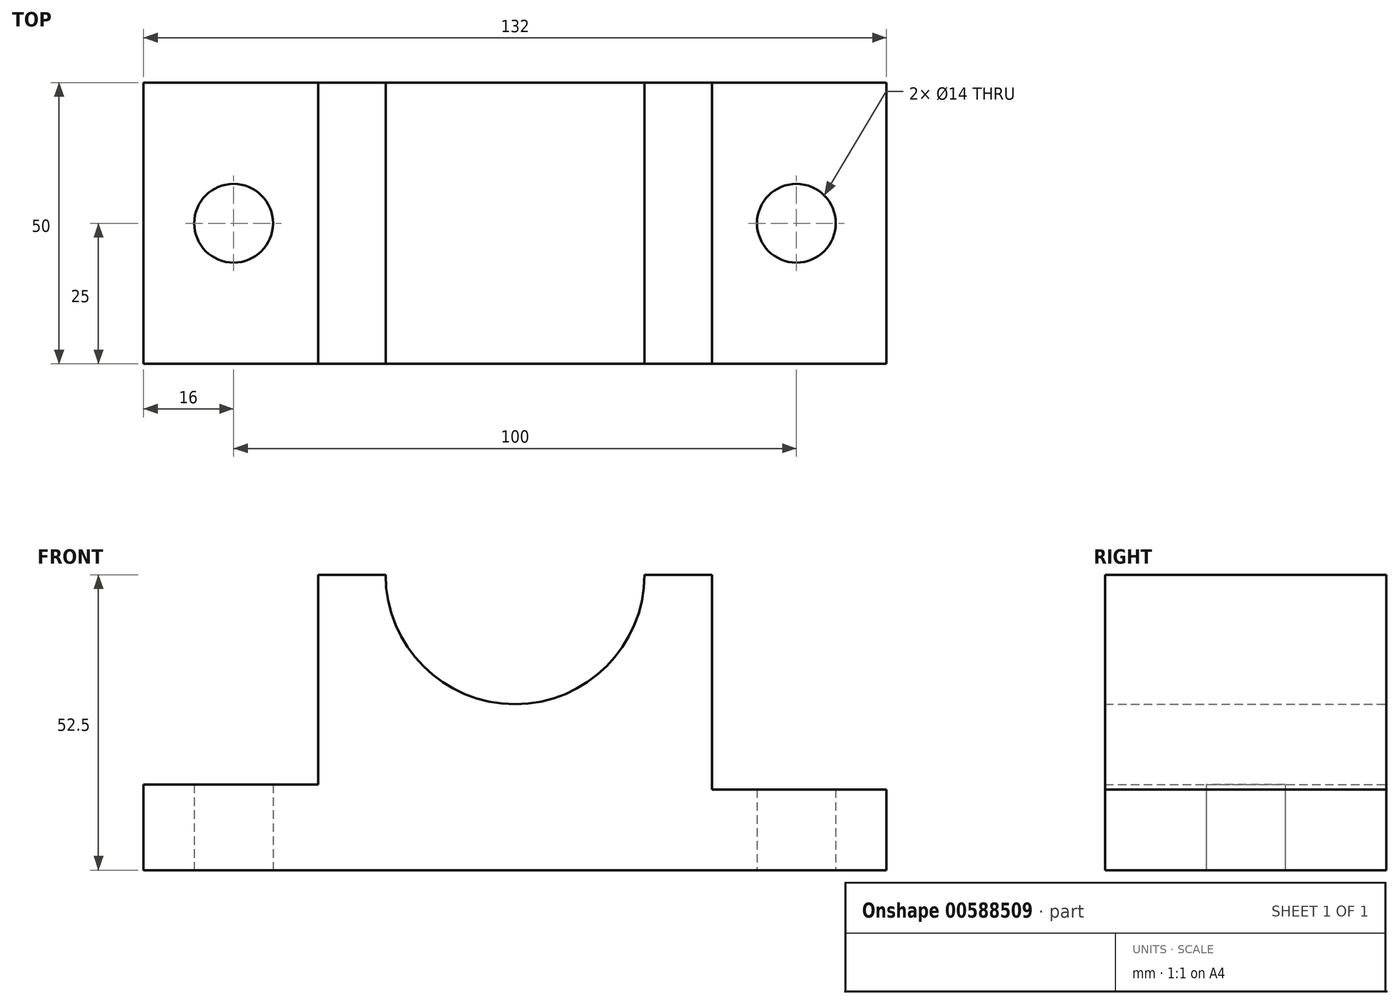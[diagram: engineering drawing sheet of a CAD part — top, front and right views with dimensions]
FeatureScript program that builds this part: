
annotation { "Feature Type Name" : "Feature", "Feature Type Description" : "" }
export const myFeature = defineFeature(function(context is Context, id is Id, definition is map)
    precondition{}
    {
        {
            var Q0;
            Q0=qCreatedBy(makeId("Front.planeOp"),FACE);
            var sketch = newSketch(context, id + "F0", { "sketchPlane" : qUnion([Q0])});
            skLineSegment(sketch, "E0", {"start": v(0, 0) * mm, "end": v(-66, 0) * mm});
            skLineSegment(sketch, "E1", {"start": v(-66, 0) * mm, "end": v(-66, 15.21) * mm});
            skLineSegment(sketch, "E2", {"start": v(-66, 15.21) * mm, "end": v(-35, 15.21) * mm});
            skLineSegment(sketch, "E3", {"start": v(-35, 15.21) * mm, "end": v(-35, 52.5) * mm});
            skLineSegment(sketch, "E4", {"start": v(-35, 52.5) * mm, "end": v(-23, 52.5) * mm});
            skLineSegment(sketch, "E5", {"start": v(23, 52.5) * mm, "end": v(35, 52.5) * mm});
            skLineSegment(sketch, "E6", {"start": v(35, 52.5) * mm, "end": v(35, 14.36) * mm});
            skLineSegment(sketch, "E7", {"start": v(35, 14.36) * mm, "end": v(66, 14.36) * mm});
            skLineSegment(sketch, "E8", {"start": v(66, 14.36) * mm, "end": v(66, 0) * mm});
            skLineSegment(sketch, "E9", {"start": v(66, 0) * mm, "end": v(0, 0) * mm});
            skArc(sketch, "E10", {"start": v(-23, 52.5) * mm, "mid": v(0, 29.5) * mm, "end": v(23, 52.5) * mm});
            skSolve(sketch);
        }
        {
            var Q0;
            Q0=makeQuery(id+"F0.imprint","IMPRINT",FACE,{"disambiguationData":[TD([[makeQuery(id+"F0.imprint","IMPRINT",EDGE,{"derivedFrom":sQuery(id+"F0.wireOp",EDGE,"E0")}),-1.0]])]});
            extrude(context, id + "F1", {"entities" : qUnion([Q0]), "depth" : 50 * mm, "offsetDistance" : 25 * mm});
        }
        {
            var Q0;
            Q0=qCreatedBy(makeId("Top.planeOp"),FACE);
            var sketch = newSketch(context, id + "F2", { "sketchPlane" : qUnion([Q0])});
            skCircle(sketch, "E11", {"center": v(-50, -25) * mm, "radius": 7 * mm});
            skCircle(sketch, "E12", {"center": v(50, -25) * mm, "radius": 7 * mm});
            skSolve(sketch);
        }
        {
            var Q0;
            Q0=makeQuery(id+"F2.imprint","IMPRINT",FACE,{"disambiguationData":[TD([[makeQuery(id+"F2.imprint","IMPRINT",EDGE,{"derivedFrom":sQuery(id+"F2.wireOp",EDGE,"E11")}),1.0]])]});
            var Q1;
            Q1=makeQuery(id+"F2.imprint","IMPRINT",FACE,{"disambiguationData":[TD([[makeQuery(id+"F2.imprint","IMPRINT",EDGE,{"derivedFrom":sQuery(id+"F2.wireOp",EDGE,"E12")}),1.0]])]});
            extrude(context, id + "F3", {"entities" : qUnion([Q0, Q1]), "operationType" : NewBodyOperationType.REMOVE, "depth" : 25 * mm, "offsetDistance" : 25 * mm});
        }
    });
